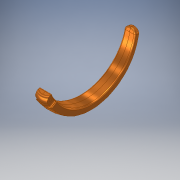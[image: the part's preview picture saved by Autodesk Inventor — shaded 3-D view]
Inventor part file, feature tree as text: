
AUTODESK INVENTOR PART (.ipt)
format: ipt  version: 2019 (Build 230136000, 136)  size: 1,212,928 bytes
history: native  units: mm
features: fillet x4, other x4, direct_edit x4, plane x3, move_body x2, extrude x1, sketch x1
ambient origin geometry x8: Origin, YZ Plane, XZ Plane, XY Plane, X Axis, Y Axis, Z Axis, Center Point
bodies: Volumenkörper1 (feature_tree), Volumenkörper3 (feature_tree), Volumenkörper2 (feature_tree), Volumenkörper4 (feature_tree)
feature tree (19):
  fillet  "Rundung1"  Radius=0.4mm
  plane  "Arbeitsebene1"
  plane  "Arbeitsebene4"
  extrude  "Extrusion1"  Depth=15.0mm
  other  "Trennen1"
  direct_edit  "Direktbearbeitung2"
  direct_edit  "Direktbearbeitung6"
  direct_edit  "Direktbearbeitung7"
  direct_edit  "Direktbearbeitung8"
  plane  "Arbeitsebene3"
  fillet  "Rundung2"  [1 undecoded]
  other  "Kombinieren1"
  fillet  "Rundung3"  Radius=1.196mm
  fillet  "Rundung4"  [1 undecoded]
  sketch  "Skizze1"  dims[d4=10.769mm d5=10.0mm d6=10.0mm d17=15.0mm d18=11.0mm d19=11.0mm d20=0.0mm d21=-0.04mm d22=0.0mm d23=1.196mm d24=0.0mm d25=0.0mm d26=90.0deg d27=1.7mm d28=0.5mm d29=0.3mm d30=90.0deg d31=4.56mm d32=0.0mm]
  other  "Skalierung2"
  other  "Skalierung3"
  move_body  "Verschieben4"
  move_body  "Verschieben5"
note: 2 required parameter values undecoded (feature->parameter linkage not recoverable at this tier; creation-order binding heuristic only, values carry confidence <= 0.55)
